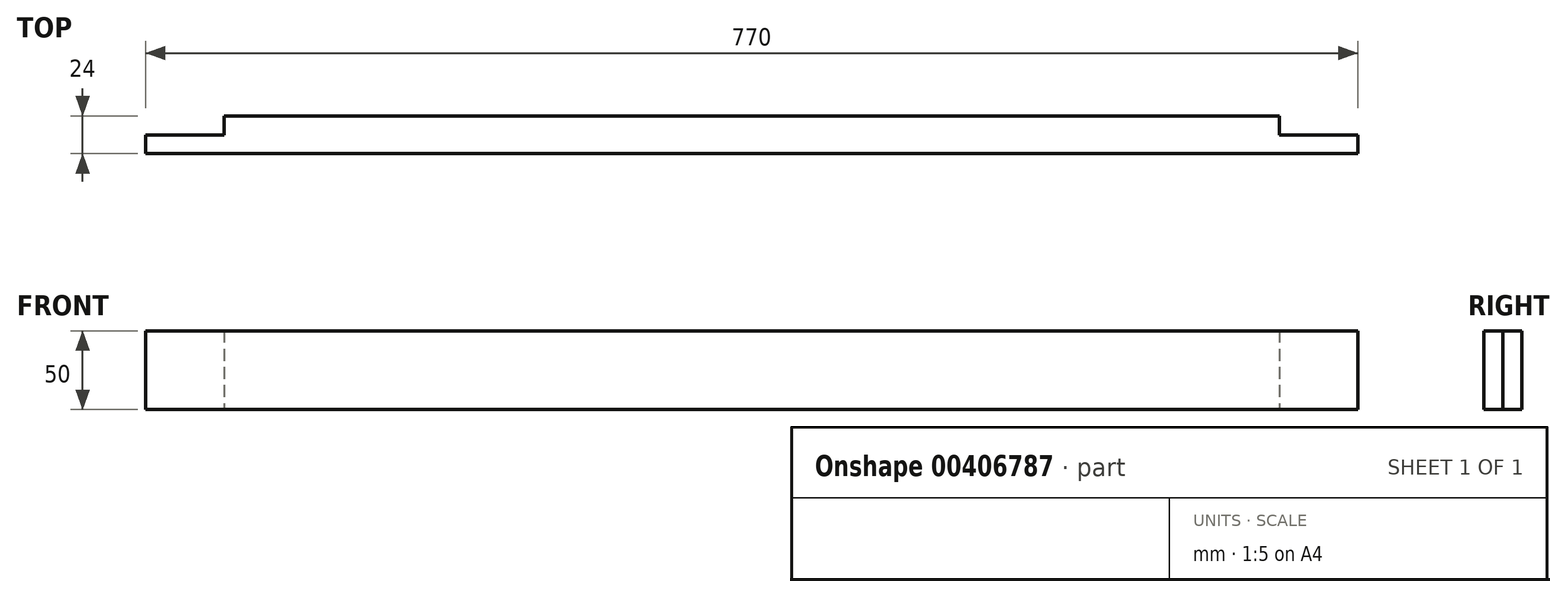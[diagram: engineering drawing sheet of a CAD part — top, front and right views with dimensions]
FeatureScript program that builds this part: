
annotation { "Feature Type Name" : "Feature", "Feature Type Description" : "" }
export const myFeature = defineFeature(function(context is Context, id is Id, definition is map)
    precondition{}
    {
        {
            var Q0;
            Q0=qCreatedBy(makeId("Front.planeOp"),FACE);
            var sketch = newSketch(context, id + "F0", { "sketchPlane" : qUnion([Q0])});
            skLineSegment(sketch, "E0.bottom", {"start": v(385, 25) * mm, "end": v(-385, 25) * mm});
            skLineSegment(sketch, "E0.top", {"start": v(385, -25) * mm, "end": v(-385, -25) * mm});
            skLineSegment(sketch, "E0.left", {"start": v(385, 25) * mm, "end": v(385, -25) * mm});
            skLineSegment(sketch, "E0.right", {"start": v(-385, 25) * mm, "end": v(-385, -25) * mm});
            skPoint(sketch, "E0.middle", {"position": v(0, 0) * mm});
            skSolve(sketch);
        }
        {
            var Q0;
            Q0 = qSketchRegion(id + "F0", true);
            extrude(context, id + "F1", {"entities" : qUnion([Q0]), "depth" : 24 * mm});
        }
        {
            var Q0;
            Q0=makeQuery(id+"F1.opExtrude","CAP_FACE",FACE,{"disambiguationData":[OSD([sQuery(id+"F0.wireOp",EDGE,"E0.bottom"),sQuery(id+"F0.wireOp",EDGE,"E0.top"),sQuery(id+"F0.wireOp",EDGE,"E0.left"),sQuery(id+"F0.wireOp",EDGE,"E0.right")])],"isStart":true});
            var sketch = newSketch(context, id + "F2", { "sketchPlane" : qUnion([Q0])});
            skLineSegment(sketch, "E1.bottom", {"start": v(-385, 25) * mm, "end": v(-335, 25) * mm});
            skLineSegment(sketch, "E1.top", {"start": v(-385, -25) * mm, "end": v(-335, -25) * mm});
            skLineSegment(sketch, "E1.left", {"start": v(-385, 25) * mm, "end": v(-385, -25) * mm});
            skLineSegment(sketch, "E1.right", {"start": v(-335, 25) * mm, "end": v(-335, -25) * mm});
            skLineSegment(sketch, "E2.bottom", {"start": v(385, 25) * mm, "end": v(335, 25) * mm});
            skLineSegment(sketch, "E2.top", {"start": v(385, -25) * mm, "end": v(335, -25) * mm});
            skLineSegment(sketch, "E2.left", {"start": v(385, 25) * mm, "end": v(385, -25) * mm});
            skLineSegment(sketch, "E2.right", {"start": v(335, 25) * mm, "end": v(335, -25) * mm});
            skSolve(sketch);
        }
        {
            var Q0;
            Q0 = qSketchRegion(id + "F2", true);
            extrude(context, id + "F3", {"entities" : qUnion([Q0]), "operationType" : NewBodyOperationType.REMOVE, "oppositeDirection" : true, "depth" : 12 * mm});
        }
    });
